# Revit family: Accessory-Cabinet_Knob-KOHLER-BEAUXLINE-K-33534_1
name_source: partatom
category: Specialty Equipment
revit_build: Autodesk Revit 2017 (Build: 20160225_1515(x64)
units: mm (PartAtom-declared; Revit-internal decimal feet)

## family parameters
Cut with Voids When Loaded = No
Host = Face
OmniClass Number = 23.31.25.00
OmniClass Title = Toilet and Bath Specialties
Part Type = Normal
Room Calculation Point = No
Round Connector Dimension = Use Diameter
Shared = No

## types (4) — shared parameters
ADA Compliant = No
Assembly Code = C1030200
Date Modified = 02/19/2021
Default Elevation = 42"
Description = BEAUXLINE CABINET KNOB 1 INCH
Height = 1 1/8"
Length = 1"
Manufacturer = KOHLER Co.
Master Format 2014 = 10 28 00
Master Format 2014 Name = Toilet, Bath, and Laundry Accessories
Material = Premium Metal Construction
Product Documentation Link = https://www.us.kohler.com
Product Name = BEAUXLINE
Product Page URL = http://www.us.kohler.com
URL = https://www.us.kohler.com
WaterSense Certified = No
Width = 1 1/8"

## per-type parameters (varying)
| type | Finish | Model | Type |
| HF1-Polished Chrome | KOHLER-Metal-HF1-Chrome | K-33534-HF1 | 1 |
| HF3-Matte Black | KOHLER-Metal-HF3-Black | K-33534-HF3 | 2 |
| HF4-Brushed Nickel | KOHLER-Metal-HF4-Brushed_Nickel | K-33534-HF4 | 3 |
| HF6-Modern Brushed Brass | KOHLER-Metal-HF6-Modern_Brushed_Brass | K-33534-HF6 | 4 |

## geometry (parser evidence)
native form markers: Sweep x5
no freeform markers — native parametric forms only
